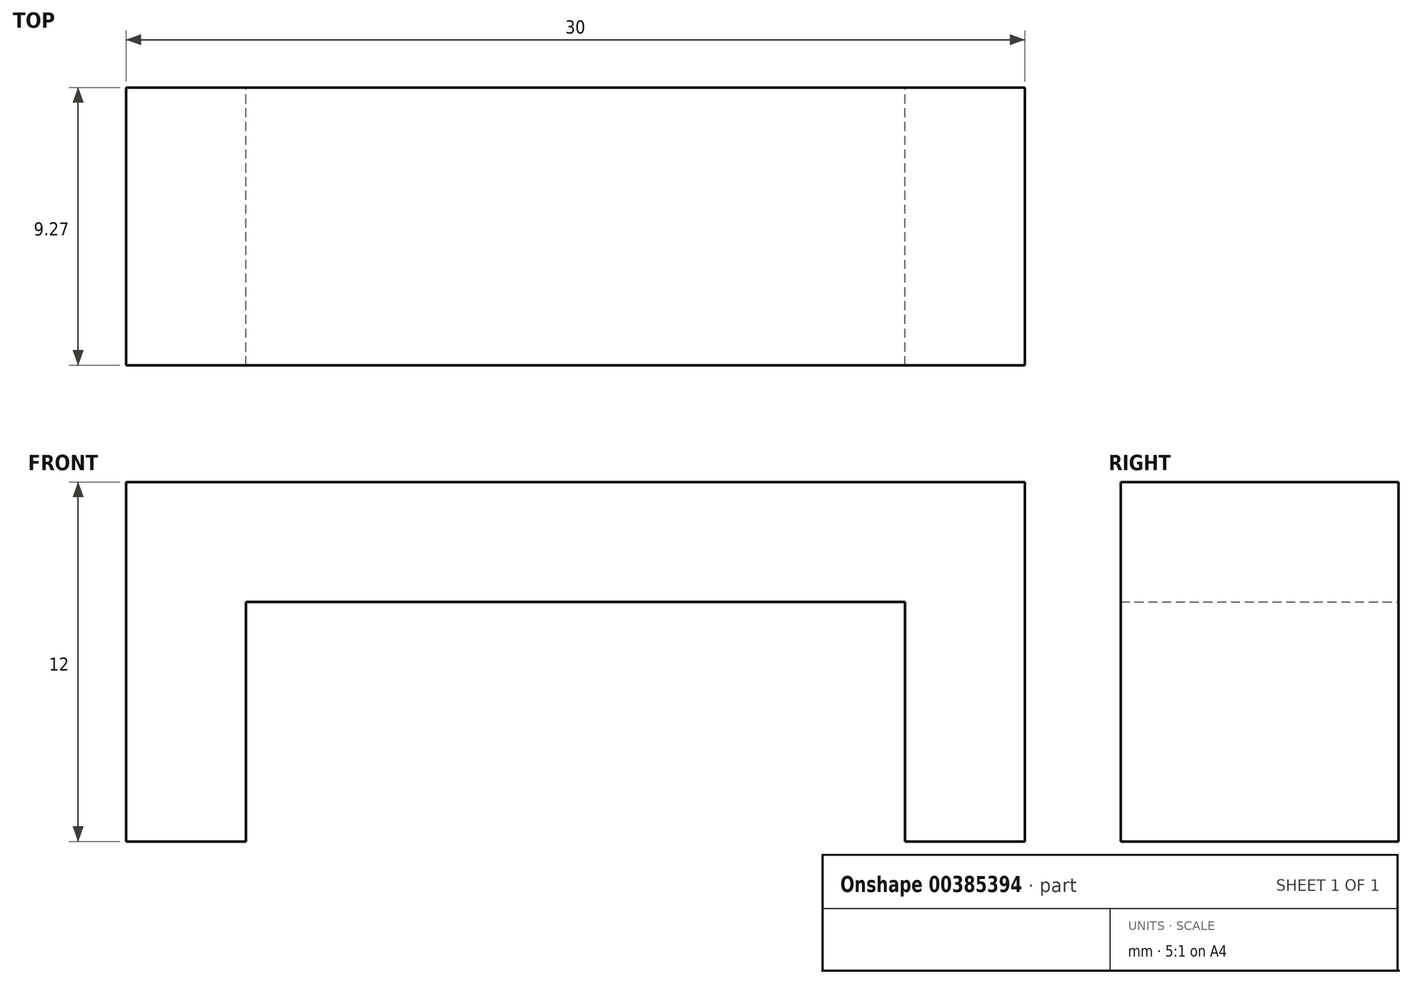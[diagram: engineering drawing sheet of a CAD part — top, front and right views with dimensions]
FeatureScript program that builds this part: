
annotation { "Feature Type Name" : "Feature", "Feature Type Description" : "" }
export const myFeature = defineFeature(function(context is Context, id is Id, definition is map)
    precondition{}
    {
        {
            var Q0;
            Q0=qCreatedBy(makeId("Front.planeOp"),FACE);
            var sketch = newSketch(context, id + "F0", { "sketchPlane" : qUnion([Q0])});
            skLineSegment(sketch, "E0", {"start": v(-11, 3) * mm, "end": v(11, 3) * mm});
            skLineSegment(sketch, "E1", {"start": v(11, 3) * mm, "end": v(11, -5) * mm});
            skLineSegment(sketch, "E2", {"start": v(11, -5) * mm, "end": v(15, -5) * mm});
            skLineSegment(sketch, "E3", {"start": v(15, -5) * mm, "end": v(15, 7) * mm});
            skLineSegment(sketch, "E4", {"start": v(15, 7) * mm, "end": v(-15, 7) * mm});
            skLineSegment(sketch, "E5", {"start": v(-15, 7) * mm, "end": v(-15, -5) * mm});
            skLineSegment(sketch, "E6", {"start": v(-15, -5) * mm, "end": v(-11, -5) * mm});
            skLineSegment(sketch, "E7", {"start": v(-11, -5) * mm, "end": v(-11, 3) * mm});
            skSolve(sketch);
        }
        {
            var Q0;
            Q0=makeQuery(id+"F0.imprint","IMPRINT",FACE,{"disambiguationData":[TD([[makeQuery(id+"F0.imprint","IMPRINT",EDGE,{"derivedFrom":sQuery(id+"F0.wireOp",EDGE,"E0")}),1.0]])]});
            extrude(context, id + "F1", {"entities" : qUnion([Q0]), "depth" : 9.27 * mm});
        }
    });
